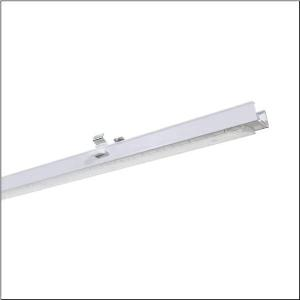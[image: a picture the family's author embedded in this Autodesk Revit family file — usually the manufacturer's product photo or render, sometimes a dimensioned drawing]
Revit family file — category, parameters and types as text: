
# Revit family: trunking_flex_31_51re12mb48b
name_source: partatom
category: Lighting Fixtures
units: mm (PartAtom-declared; Revit-internal decimal feet)

## family parameters
Cut with Voids When Loaded = No
Host = Face
Light Source = No
Part Type = Normal
Room Calculation Point = No
Round Connector Dimension = Use Diameter
Shared = No

## types (1)
- --- (1 x LED, 8000 lm, 50 W, 4000K)
    Apparent Load = 50 VA
    CIE Flux Codes = 65 91 98 99 100
    Color Rendering = 80
    Color Temperature = 4000K
    Default Elevation = 1800 mm
    Description = Trunking Flex 31, luminaire insert, of extruded aluminium section, coated, traffic white (RAL 9016), length: 1.472mm, width: 91mm, height: 53mm, LED rated luminous flux: 8.000lm, light colour: 840, control gear: ON/OFF Multilumen, with system connector: socket, mains connection: 220..240V, AC, 50/60Hz, rated input power: 50W, luminous flux adjustable on luminaire in four steps (4130/5610/6850/8000lm), connected load according to luminous flux setting (25/34/42/50W), primary light control with lens, of plastic, primary optical cover: cover, of PMMA, light emission: direct distribution, protection rating (complete): IP20, insulation class (complete): insulation class I (protective earthing), certification: CE, UKCA, impact resistance: IK02, permissible ambient temperature for indoor applications: -20..+40°C, packaging unit: 1 piece
    Height = 58 mm
    Lamp = 1 x LED
    Lamp Light Flux = 8000 lm
    Lamp Power = 50 W
    Lamp count = 1
    Length = 1472 mm
    Luminous efficacy = 160 lm/W
    Manufacturer = Siteco
    ModVariant = No
    Model = 51RE12MB48B
    Mounting Place = Ceiling
    Mounting Type = Pendant
    Number of Poles = 1
    OnlyDefault = Yes
    Power Factor = 1
    Product Name = Trunking Flex 31
    Product group = luminaire insert
    ProductGroupID = 901
    Protection Class = Protection class I
    Protection Degree = IP 20
    RLX_Detail_Level = 1
    RLX_Emergency_Light_Flux = 0 lm
    RLX_Emergency_Type = 0
    RLX_Emergency_Type_DB = No
    RlxData = <blob elided: 20289 chars, md5=431c4018>
    Socket = socket
    Standby Power = 0 W
    System Light Flux = 8000 lm
    System Power = 50 W
    Type Comments = factory setting: luminous flux: 100 % | (ON | ON) | 300 mA
    Type Image = l_1266702.jpg
    URL = http://relux.com
    VarID = @adj_027123
    Voltage = 0 V
    Weight = 0.00 kg
    Width = 65 mm

## geometry (parser evidence)
native form markers: Blend x4, Sweep x13
no freeform markers — native parametric forms only
